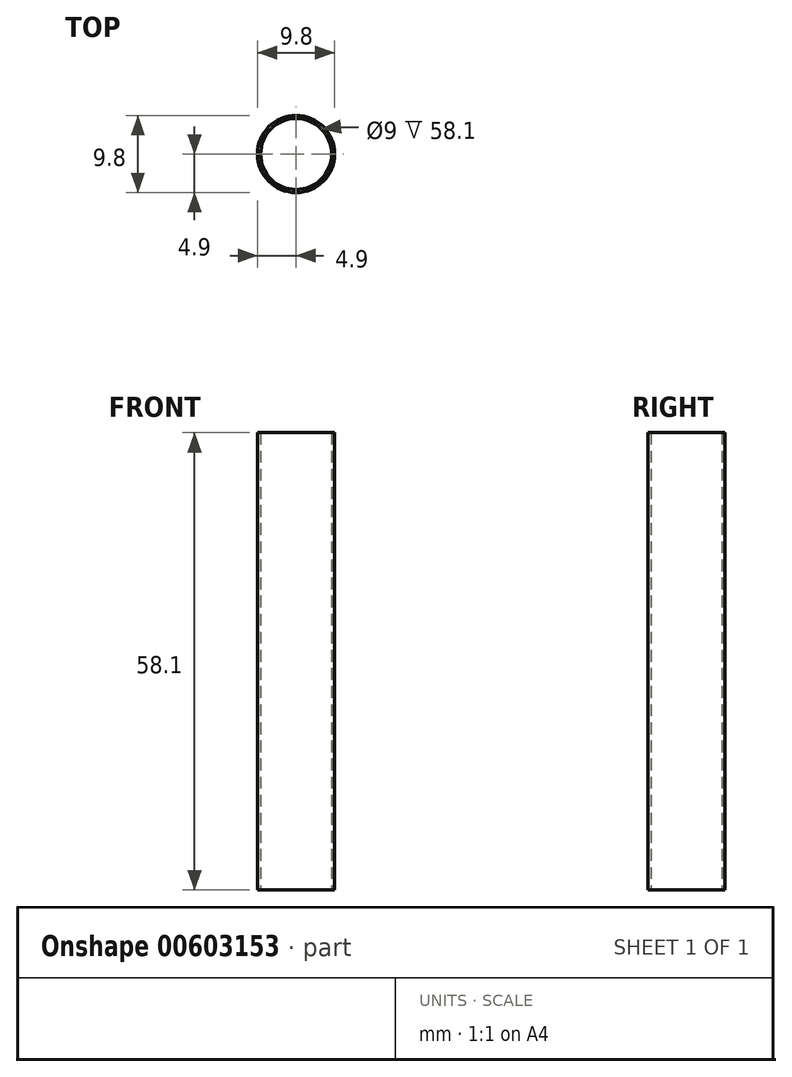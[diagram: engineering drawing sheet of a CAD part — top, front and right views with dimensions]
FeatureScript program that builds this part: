
annotation { "Feature Type Name" : "Feature", "Feature Type Description" : "" }
export const myFeature = defineFeature(function(context is Context, id is Id, definition is map)
    precondition{}
    {
        {
            var Q0;
            Q0=qCreatedBy(makeId("Top.planeOp"),FACE);
            var sketch = newSketch(context, id + "F0", { "sketchPlane" : qUnion([Q0])});
            skCircle(sketch, "E0", {"center": v(0, 0) * mm, "radius": 4.9 * mm});
            skCircle(sketch, "E1", {"center": v(0, 0) * mm, "radius": 4.5 * mm});
            skSolve(sketch);
        }
        {
            var Q0;
            Q0=makeQuery(id+"F0.imprint","IMPRINT",FACE,{"disambiguationData":[TD([[makeQuery(id+"F0.imprint","IMPRINT",EDGE,{"derivedFrom":sQuery(id+"F0.wireOp",EDGE,"E0")}),1.0]])]});
            extrude(context, id + "F1", {"entities" : qUnion([Q0]), "depth" : 58.1 * mm, "offsetDistance" : 25 * mm});
        }
    });
